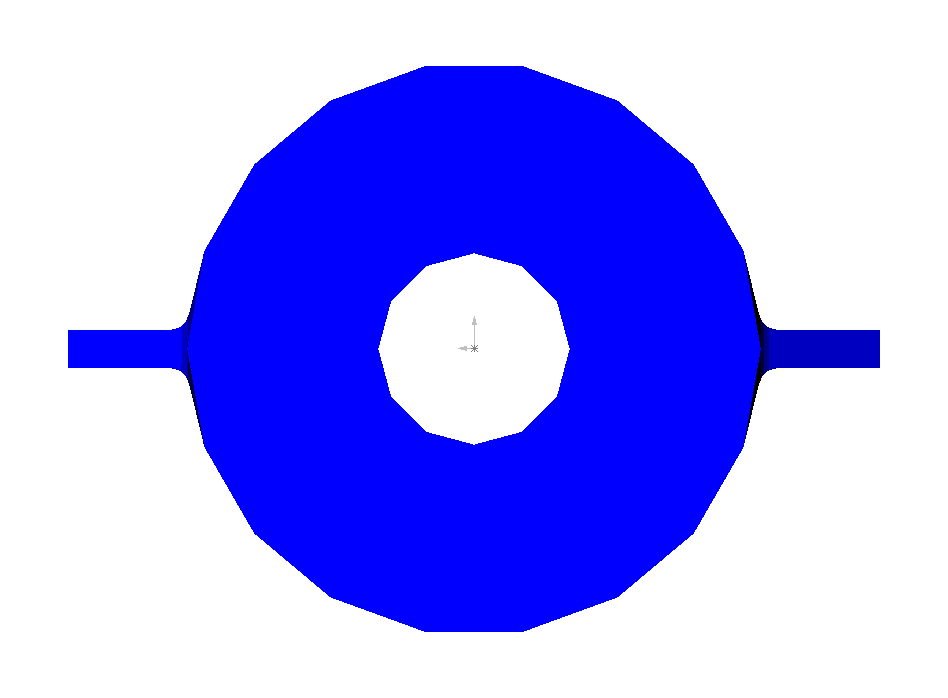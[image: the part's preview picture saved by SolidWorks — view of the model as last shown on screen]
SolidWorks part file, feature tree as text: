
SOLIDWORKS PART (.sldprt)
format: sldprt  version: not decoded by parser v0  size: 140,288 bytes
history: native  units: mm
features: sketch x5, plane x3, extrude x3, fillet x2, mirror x2, cut_extrude x2, material x1 (+9 scaffold rows collapsed)
feature tree (27):
  scaffold x9  (default folders/planes/origin — collapsed)
  material  "Material <not specified>"
  plane  "Plane1"
  plane  "Plane2"
  plane  "Plane3"
  sketch  "Sketch1"  dims[D1=120.0mm]
  extrude  "Base-Extrude"  Depth=25mm
  sketch  "Sketch2"  dims[c1.D1=16.0mm c1.D2=20.0mm c2.D1=55.0mm c2.D2=16.0mm c2.D3=12.5mm c2.D4=22.5mm c2.D5=~30.696091mm]
  extrude  "Boss-Extrude1"  Depth=8mm
  fillet  "Fillet1"  Radius=4mm
  mirror  "Mirror1"
  fillet  "Fillet2"  Radius=4mm
  sketch  "Sketch3"  dims[D1=50.0mm]
  extrude  "Boss-Extrude2"  Depth=450mm
  sketch  "Sketch5"  dims[c1.D1=10.0mm c1.D2=5.0mm c1.D3=5.0mm c1.D4=5.0mm c2.D2=3.0mm c2.D3=78.0mm]
  cut_extrude  "Cut-Extrude1"  [1 undecoded]
  mirror  "Mirror2"
  sketch  "Sketch6"
  cut_extrude  "Cut-Extrude2"  [1 undecoded]
decode coverage: 9 of 14 modeling features carry decoded parameters
note: ~ marks probable driven/reference dimensions
note: 2 parameter values undecoded
note: suppression state not decoded; provenance and decode notes live in map.json
